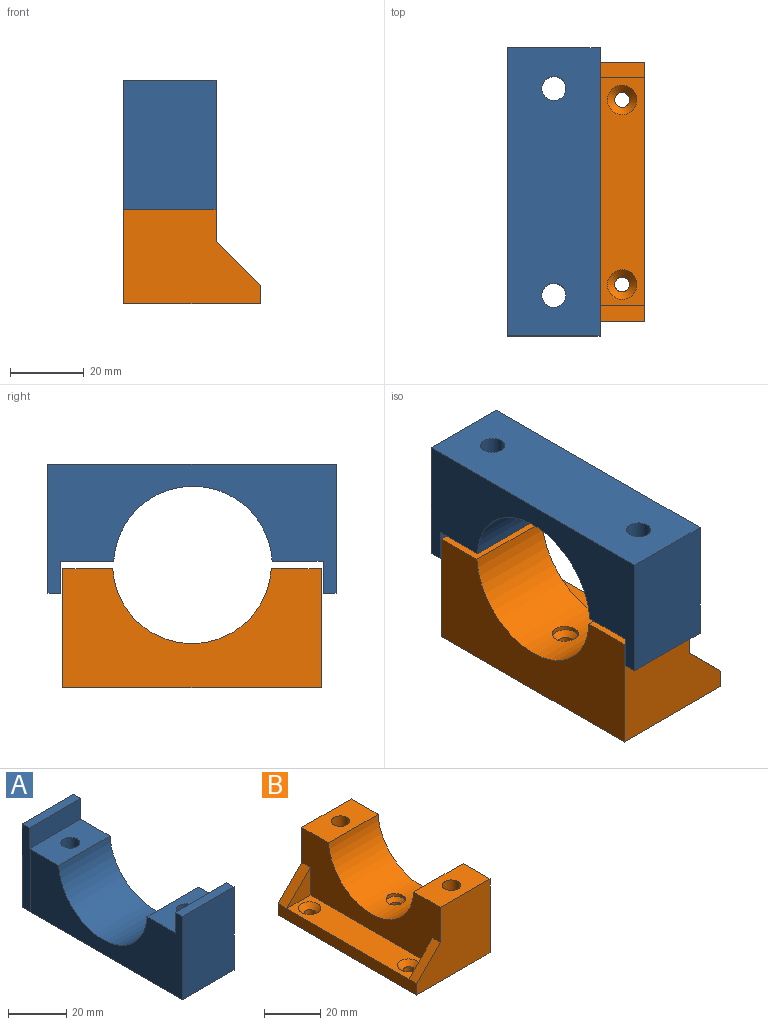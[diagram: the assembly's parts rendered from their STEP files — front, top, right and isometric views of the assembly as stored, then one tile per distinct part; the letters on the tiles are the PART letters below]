
ASSEMBLY  parts=2 mates=1
PART A: 16 faces, bbox 25x78x35 mm
  f0: plane 25x13.78mm, normal (0,0,1), area 311.4mm2, adj f1,f2,f4,f9,f13
  f1: plane 74x35mm, normal (-1,0,0), area 1302.1mm2, adj f0,f5,f7,f8,f9,f13,f14,f15
  f2: plane 78x35mm, normal (1,0,0), area 1437.8mm2, adj f0,f7,f8,f9,f10,f11,f12,f13
  f3: plane 35x4mm, normal (-1,0,0), area 135.6mm2, adj f5,f7,f8,f10,f11,f12
  f4: cylinder r=3.25mm len=26.3mm, axis (0,0,-1), area 537.1mm2, adj f0,f8
  f5: plane 26.3x0.01mm, normal (0,-1,0), area 0.2mm2, adj f1,f3,f7,f8
  f6: cylinder r=3.25mm len=26.3mm, axis (0,0,-1), area 537.1mm2, adj f7,f8
  f7: plane 25.01x14.28mm, normal (0,0,1), area 323.9mm2, adj f1,f2,f3,f5,f6,f9,f10
  f8: plane 78x25.01mm, normal (0,0,-1), area 1883.7mm2, adj f1,f2,f3,f4,f5,f6,f11,f14
  f9: cylinder r=21.5mm len=42.93mm, axis (-1,0,0), area 1628.6mm2, adj f0,f1,f2,f7
  f10: plane 25.01x8.7mm, normal (0,-1,0), area 217.6mm2, adj f2,f3,f7,f12
  f11: plane 35x25.01mm, normal (0,1,0), area 875.3mm2, adj f2,f3,f8,f12
  f12: plane 25.01x3.5mm, normal (0,0,1), area 87.5mm2, adj f2,f3,f10,f11
  f13: plane 25x8.7mm, normal (0,1,0), area 217.5mm2, adj f0,f1,f2,f15
  f14: plane 35x25mm, normal (0,-1,0), area 875mm2, adj f1,f2,f8,f15
  f15: plane 25x3.5mm, normal (0,0,1), area 87.5mm2, adj f1,f2,f13,f14
PART B: 37 faces, bbox 37x70x32.3 mm
  f0: plane 70x27.3mm, normal (-1,0,0), area 1136mm2, adj f13,f15,f17,f18,f20,f26,f27,f28
  f1: plane 6.06x6mm, normal (0,-1,0), area 36.4mm2, adj f2,f6,f19,f24
  f2: plane 6x5.25mm, normal (-0.87,-0.5,0), area 36.4mm2, adj f1,f3,f19,f24
  f3: plane 6x5.25mm, normal (-0.87,0.5,0), area 36.4mm2, adj f2,f4,f19,f24
  f4: plane 6.06x6mm, normal (0,1,0), area 36.4mm2, adj f3,f5,f19,f24
  f5: plane 6x5.25mm, normal (0.87,0.5,0), area 36.4mm2, adj f4,f6,f19,f24
  f6: plane 6x5.25mm, normal (0.87,-0.5,0), area 36.4mm2, adj f1,f5,f19,f24
  f7: plane 6x5.25mm, normal (-0.87,-0.5,0), area 36.4mm2, adj f8,f12,f19,f22
  f8: plane 6x5.25mm, normal (-0.87,0.5,0), area 36.4mm2, adj f7,f9,f19,f22
  f9: plane 6.06x6mm, normal (0,1,0), area 36.4mm2, adj f8,f10,f19,f22
  f10: plane 6x5.25mm, normal (0.87,0.5,0), area 36.4mm2, adj f9,f11,f19,f22
  f11: plane 6x5.25mm, normal (0.87,-0.5,0), area 36.4mm2, adj f10,f12,f19,f22
  f12: plane 6.06x6mm, normal (0,-1,0), area 36.4mm2, adj f7,f11,f19,f22
  f13: plane 25x13.53mm, normal (0,0,1), area 305.2mm2, adj f0,f14,f17,f20,f23
  f14: plane 70x32.3mm, normal (1,0,0), area 1586.5mm2, adj f13,f15,f17,f18,f19,f20
  f15: plane 37x32.3mm, normal (0,1,0), area 939.5mm2, adj f0,f14,f18,f19,f25,f30
  f16: cylinder r=3.5mm len=7mm, axis (0,0,-1), area 25.1mm2, adj f20,f34
  f17: plane 37x32.3mm, normal (0,-1,0), area 939.5mm2, adj f0,f13,f14,f19,f25,f29
  f18: plane 25x13.53mm, normal (0,0,1), area 305.2mm2, adj f0,f14,f15,f20,f21
  f19: plane 70x37mm, normal (0,0,-1), area 2361.3mm2, adj f1,f2,f3,f4,f5,f6,f7,f8
  f20: cylinder r=21.5mm len=42.93mm, axis (-1,0,0), area 1590.1mm2, adj f0,f13,f14,f16,f18
  f21: cylinder r=3.25mm len=26.3mm, axis (0,0,-1), area 537.1mm2, adj f18,f22
  f22: plane 12.12x10.5mm, normal (0,0,-1), area 62.3mm2, adj f7,f8,f9,f10,f11,f12,f21
  f23: cylinder r=3.25mm len=26.3mm, axis (0,0,-1), area 537.1mm2, adj f13,f24
  f24: plane 12.12x10.5mm, normal (0,0,-1), area 62.3mm2, adj f1,f2,f3,f4,f5,f6,f23
  f25: plane 70x5mm, normal (-1,0,0), area 350mm2, adj f15,f17,f19,f26,f29,f30
  f26: plane 61.63x12mm, normal (0,0,1), area 639mm2, adj f0,f25,f27,f28,f35,f36
  f27: plane 12x12mm, normal (0,-1,0), area 72mm2, adj f0,f26,f30
  f28: plane 12x12mm, normal (0,1,0), area 72mm2, adj f0,f26,f29
  f29: plane 12x12mm, normal (-0.71,0,0.71), area 67.9mm2, adj f0,f17,f25,f28
  f30: plane 12x12mm, normal (-0.71,0,0.71), area 74.2mm2, adj f0,f15,f25,f27
  f31: cylinder r=2mm len=4mm, axis (0,0,-1), area 37.7mm2, adj f19,f35
  f32: cylinder r=2mm len=4mm, axis (0,0,-1), area 37.7mm2, adj f19,f36
  f33: cylinder r=2mm len=9.5mm, axis (0,0,-1), area 119.4mm2, adj f19,f34
  f34: cone r=1.5mm half-angle=45deg, axis (0,0,1), area 36.7mm2, adj f16,f33
  f35: cone r=2mm half-angle=45deg, axis (0,0,1), area 53.3mm2, adj f26,f31
  f36: cone r=2mm half-angle=45deg, axis (0,0,1), area 53.3mm2, adj f26,f32
PLACE A rot(axis=(0,1,0),180deg) t=(0.91,-72.26,47.5)mm
PLACE B rot(axis=(0,0,1),180deg) t=(0.91,-72.26,-13.1)mm
MATE fastened B.f23 <-> A.f6  axis (0,0,-1) through (0.91,-44.26,19.2)mm
